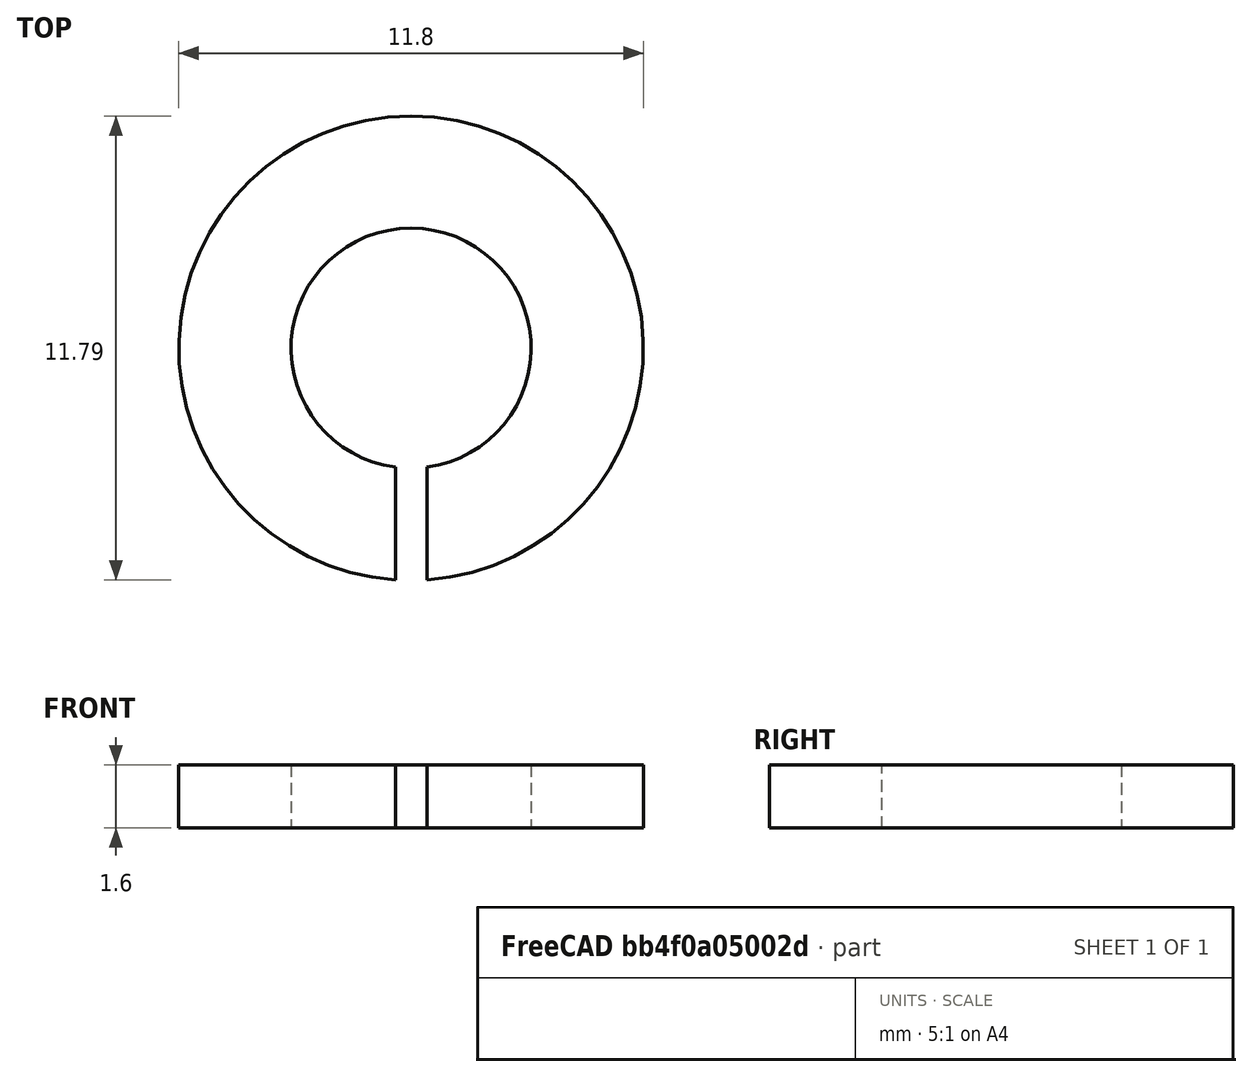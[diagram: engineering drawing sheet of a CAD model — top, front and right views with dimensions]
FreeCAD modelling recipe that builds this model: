
FCSTD DOCUMENT  (FreeCAD 0.15R4651 (Git))
Label: Federring_DIN127-A6
License: All rights reserved
LicenseURL: http://de.wikipedia.org/wiki/Alle_Rechte_vorbehalten
objects: Sketcher::SketchObject×1, PartDesign::Pad×1
note: 3 computed .brp shape members not serialized (recipe doc carries the construction recipe); baked Part::Feature solids carry a one-line shape summary decoded from their .brp

FEATURE [Sketcher::SketchObject] Sketch
  sketch-geometry (4):
    g0: ArcOfCircle CenterX=0 CenterY=0 CenterZ=0 NormalX=0 NormalY=0 NormalZ=1 Radius=3.05 StartAngle=4.84392 EndAngle=10.864
    g1: ArcOfCircle CenterX=0 CenterY=0 CenterZ=0 NormalX=0 NormalY=0 NormalZ=1 Radius=5.9 StartAngle=4.78024 EndAngle=10.9277
    g2: LineSegment StartX=0.4 StartY=-3.02366 StartZ=0 EndX=0.4 EndY=-5.88643 EndZ=0
    g3: LineSegment StartX=-0.4 StartY=-5.88643 StartZ=0 EndX=-0.4 EndY=-3.02366 EndZ=0
  constraints (12):
    c: Coincident(g0,g-1)
    c: Coincident(g1,g-1)
    c: Vertical(g2)
    c: Vertical(g3)
    c: Coincident(g0,g2)
    c: Coincident(g0,g3)
    c: Coincident(g1,g2)
    c: Coincident(g1,g3)
    c: Symmetric(g1,g1,g-2)
    c: Radius(g0) = 3.05
    c: Radius(g1) = 5.9
    c: DistanceX(g1,g1) = -0.8
FEATURE [PartDesign::Pad] Pad  label="Federring DIN 127-A 6 #"
  Length = 1.6
  Length2 = 100
  Midplane = true
  Sketch = -> Sketch
  Type = 0
